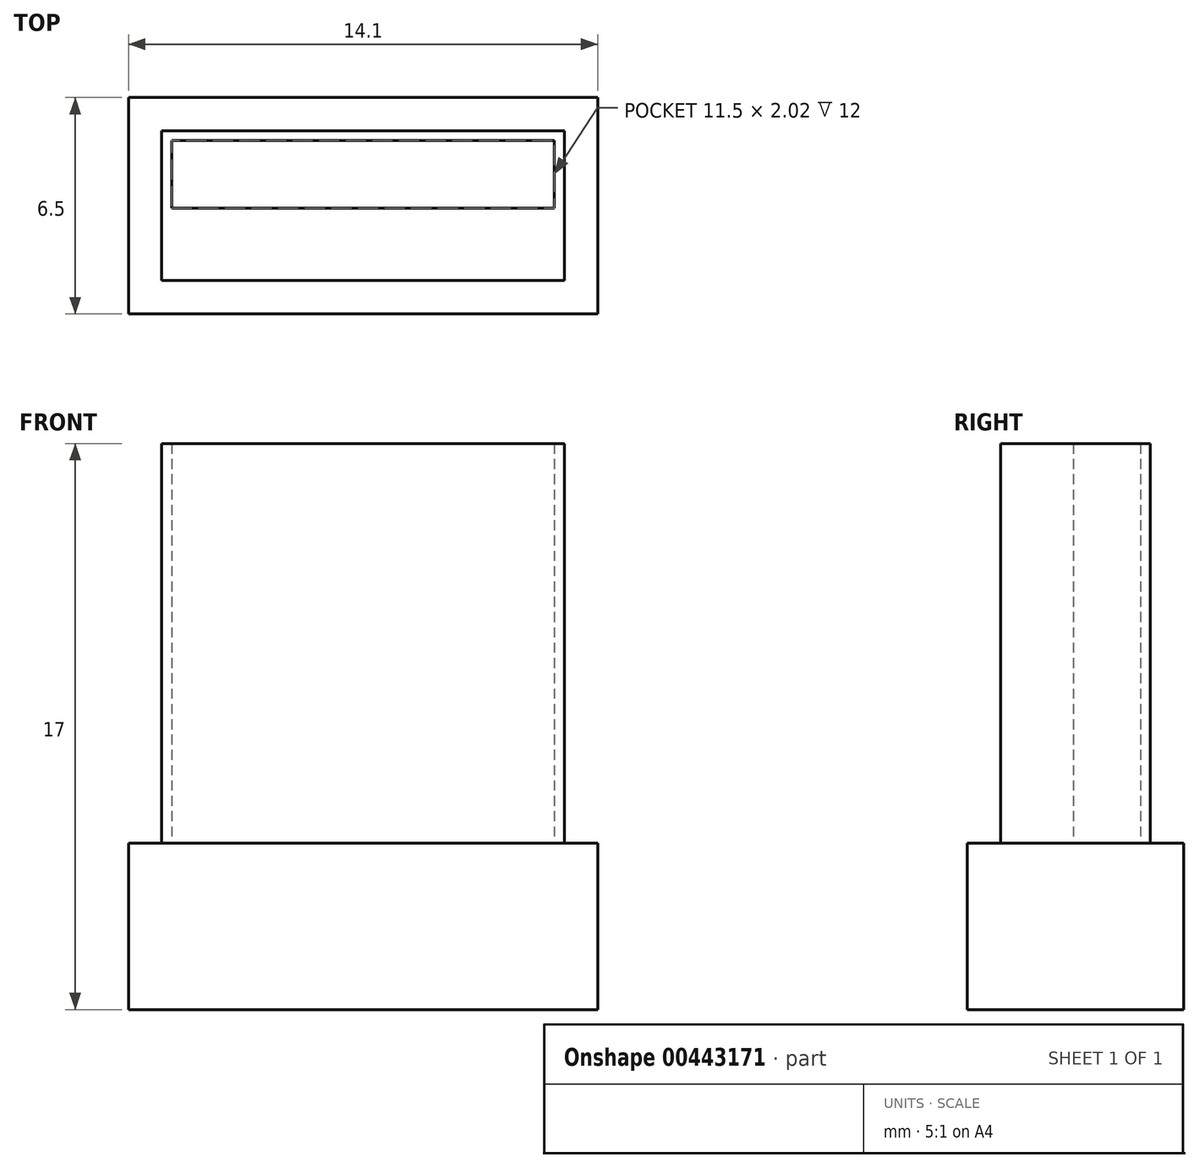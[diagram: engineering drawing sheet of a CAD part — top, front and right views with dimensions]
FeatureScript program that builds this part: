
annotation { "Feature Type Name" : "Feature", "Feature Type Description" : "" }
export const myFeature = defineFeature(function(context is Context, id is Id, definition is map)
    precondition{}
    {
        {
            var Q0;
            Q0=qCreatedBy(makeId("Top.planeOp"),FACE);
            var sketch = newSketch(context, id + "F0", { "sketchPlane" : qUnion([Q0])});
            skLineSegment(sketch, "E0.bottom", {"start": v(0, 0) * mm, "end": v(12.1, 0) * mm});
            skLineSegment(sketch, "E0.top", {"start": v(0, 4.5) * mm, "end": v(12.1, 4.5) * mm});
            skLineSegment(sketch, "E0.left", {"start": v(0, 0) * mm, "end": v(0, 4.5) * mm});
            skLineSegment(sketch, "E0.right", {"start": v(12.1, 0) * mm, "end": v(12.1, 4.5) * mm});
            skLineSegment(sketch, "E1.0", {"start": v(0.3, 4.2) * mm, "end": v(11.8, 4.2) * mm});
            skLineSegment(sketch, "E1.1", {"start": v(0.3, 0.3) * mm, "end": v(0.3, 4.2) * mm});
            skLineSegment(sketch, "E1.2", {"start": v(0.3, 0.3) * mm, "end": v(11.8, 0.3) * mm});
            skLineSegment(sketch, "E1.3", {"start": v(11.8, 0.3) * mm, "end": v(11.8, 4.2) * mm});
            skSolve(sketch);
        }
        {
            var Q0;
            Q0=makeQuery(id+"F0.imprint","IMPRINT",FACE,{"disambiguationData":[TD([[makeQuery(id+"F0.imprint","IMPRINT",EDGE,{"derivedFrom":sQuery(id+"F0.wireOp",EDGE,"E0.bottom")}),1.0]])]});
            extrude(context, id + "F1", {"entities" : qUnion([Q0]), "depth" : 12 * mm});
        }
        {
            var Q0;
            Q0=qCreatedBy(makeId("Top.planeOp"),FACE);
            var sketch = newSketch(context, id + "F2", { "sketchPlane" : qUnion([Q0])});
            skLineSegment(sketch, "E2.bottom", {"start": v(0.3, 0.3) * mm, "end": v(11.8, 0.3) * mm});
            skLineSegment(sketch, "E2.top", {"start": v(0.3, 2.18) * mm, "end": v(11.8, 2.18) * mm});
            skLineSegment(sketch, "E2.left", {"start": v(0.3, 0.3) * mm, "end": v(0.3, 2.18) * mm});
            skLineSegment(sketch, "E2.right", {"start": v(11.8, 0.3) * mm, "end": v(11.8, 2.18) * mm});
            skSolve(sketch);
        }
        {
            var Q0;
            Q0=makeQuery(id+"F2.imprint","IMPRINT",FACE,{"disambiguationData":[TD([[makeQuery(id+"F2.imprint","IMPRINT",EDGE,{"derivedFrom":sQuery(id+"F2.wireOp",EDGE,"E2.bottom")}),1.0]])]});
            extrude(context, id + "F3", {"entities" : qUnion([Q0]), "operationType" : NewBodyOperationType.ADD, "depth" : 12 * mm});
        }
        {
            var Q0;
            Q0=makeQuery(id+"F3.boolean.opBoolean","MERGE",FACE,{"derivedFrom":[makeQuery(id+"F1.opExtrude","CAP_FACE",FACE,{"disambiguationData":[OSD([sQuery(id+"F0.wireOp",EDGE,"E0.bottom"),sQuery(id+"F0.wireOp",EDGE,"E0.top"),sQuery(id+"F0.wireOp",EDGE,"E0.left"),sQuery(id+"F0.wireOp",EDGE,"E0.right"),sQuery(id+"F0.wireOp",EDGE,"E1.0"),sQuery(id+"F0.wireOp",EDGE,"E1.1"),sQuery(id+"F0.wireOp",EDGE,"E1.2"),sQuery(id+"F0.wireOp",EDGE,"E1.3")])],"isStart":true}),makeQuery(id+"F3.opExtrude","CAP_FACE",FACE,{"disambiguationData":[OSD([sQuery(id+"F2.wireOp",EDGE,"E2.bottom"),sQuery(id+"F2.wireOp",EDGE,"E2.top"),sQuery(id+"F2.wireOp",EDGE,"E2.left"),sQuery(id+"F2.wireOp",EDGE,"E2.right")])],"isStart":true})]});
            var sketch = newSketch(context, id + "F4", { "sketchPlane" : qUnion([Q0])});
            skLineSegment(sketch, "E3.0", {"start": v(-1.03, 1.03) * mm, "end": v(13.13, 1.03) * mm});
            skLineSegment(sketch, "E3.1", {"start": v(-1.03, 1.03) * mm, "end": v(-1.03, -5.53) * mm});
            skLineSegment(sketch, "E3.2", {"start": v(-1.03, -5.53) * mm, "end": v(13.13, -5.53) * mm});
            skLineSegment(sketch, "E3.3", {"start": v(13.13, 1.03) * mm, "end": v(13.13, -5.53) * mm});
            skSolve(sketch);
        }
        {
            var Q0;
            Q0=makeQuery(id+"F4.imprint","IMPRINT",FACE,{"disambiguationData":[TD([[makeQuery(id+"F4.imprint","IMPRINT",EDGE,{"derivedFrom":sQuery(id+"F4.wireOp",EDGE,"E3.0")}),-1.0]])]});
            extrude(context, id + "F5", {"entities" : qUnion([Q0]), "depth" : 5 * mm});
        }
        {
            var Q0;
            Q0=makeQuery(id+"F5.opExtrude","SWEPT_BODY",BODY,{"disambiguationData":[OSD([sQuery(id+"F0.wireOp",EDGE,"E0.bottom"),sQuery(id+"F0.wireOp",EDGE,"E0.top"),sQuery(id+"F0.wireOp",EDGE,"E0.left"),sQuery(id+"F0.wireOp",EDGE,"E0.right"),sQuery(id+"F4.wireOp",EDGE,"E3.0"),sQuery(id+"F4.wireOp",EDGE,"E3.1"),sQuery(id+"F4.wireOp",EDGE,"E3.2"),sQuery(id+"F4.wireOp",EDGE,"E3.3")])]});
            deleteBodies(context, id + "F6", {"entities" : qUnion([Q0])});
        }
        {
            var Q0;
            Q0=makeQuery(id+"F3.boolean.opBoolean","MERGE",FACE,{"derivedFrom":[makeQuery(id+"F1.opExtrude","CAP_FACE",FACE,{"disambiguationData":[OSD([sQuery(id+"F0.wireOp",EDGE,"E0.bottom"),sQuery(id+"F0.wireOp",EDGE,"E0.top"),sQuery(id+"F0.wireOp",EDGE,"E0.left"),sQuery(id+"F0.wireOp",EDGE,"E0.right"),sQuery(id+"F0.wireOp",EDGE,"E1.0"),sQuery(id+"F0.wireOp",EDGE,"E1.1"),sQuery(id+"F0.wireOp",EDGE,"E1.2"),sQuery(id+"F0.wireOp",EDGE,"E1.3")])],"isStart":true}),makeQuery(id+"F3.opExtrude","CAP_FACE",FACE,{"disambiguationData":[OSD([sQuery(id+"F2.wireOp",EDGE,"E2.bottom"),sQuery(id+"F2.wireOp",EDGE,"E2.top"),sQuery(id+"F2.wireOp",EDGE,"E2.left"),sQuery(id+"F2.wireOp",EDGE,"E2.right")])],"isStart":true})]});
            var sketch = newSketch(context, id + "F7", { "sketchPlane" : qUnion([Q0])});
            skLineSegment(sketch, "E4.bottom", {"start": v(13.1, 1) * mm, "end": v(-1, 1) * mm});
            skLineSegment(sketch, "E4.top", {"start": v(13.1, -5.5) * mm, "end": v(-1, -5.5) * mm});
            skLineSegment(sketch, "E4.left", {"start": v(13.1, 1) * mm, "end": v(13.1, -5.5) * mm});
            skLineSegment(sketch, "E4.right", {"start": v(-1, 1) * mm, "end": v(-1, -5.5) * mm});
            skSolve(sketch);
        }
        {
            var Q0;
            Q0 = qSketchRegion(id + "F7", true);
            extrude(context, id + "F8", {"entities" : qUnion([Q0]), "operationType" : NewBodyOperationType.ADD, "depth" : 5 * mm});
        }
    });
